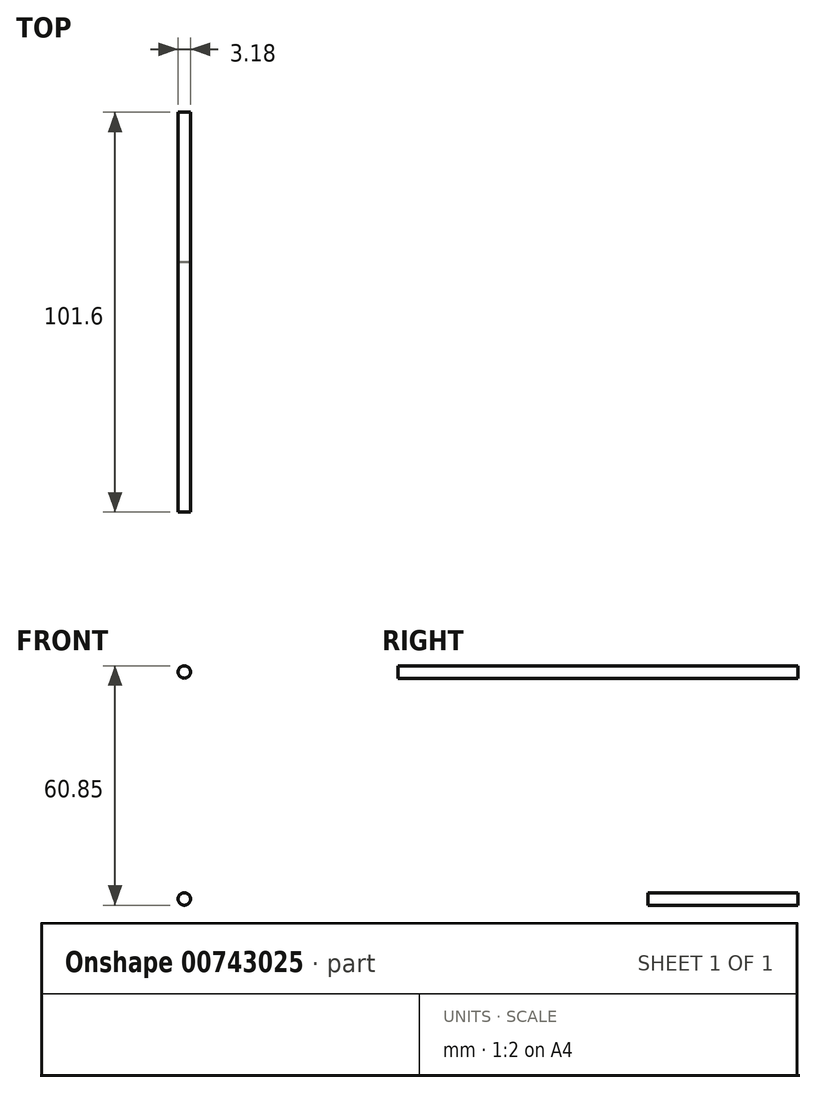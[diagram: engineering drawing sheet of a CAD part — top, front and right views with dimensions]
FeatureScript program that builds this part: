
annotation { "Feature Type Name" : "Feature", "Feature Type Description" : "" }
export const myFeature = defineFeature(function(context is Context, id is Id, definition is map)
    precondition{}
    {
        {
            var Q0;
            Q0=qCreatedBy(makeId("Front.planeOp"),FACE);
            var sketch = newSketch(context, id + "F0", { "sketchPlane" : qUnion([Q0])});
            skLineSegment(sketch, "E0", {"start": v(0, 0) * mm, "end": v(0, 8.52) * mm});
            skCircle(sketch, "E1", {"center": v(0, 8.52) * mm, "radius": 1.59 * mm});
            skLineSegment(sketch, "E2", {"start": v(0, 0) * mm, "end": v(0, -27.75) * mm});
            skCircle(sketch, "E3", {"center": v(0, -27.75) * mm, "radius": 1.59 * mm});
            skLineSegment(sketch, "E4", {"start": v(0, -27.75) * mm, "end": v(0, -49.15) * mm});
            skCircle(sketch, "E5", {"center": v(0, -49.15) * mm, "radius": 1.59 * mm});
            skSolve(sketch);
        }
        {
            var Q0;
            Q0=makeQuery(id+"F0.imprint","IMPRINT",FACE,{"disambiguationData":[TD([[makeQuery(id+"F0.imprint","IMPRINT",EDGE,{"derivedFrom":sQuery(id+"F0.wireOp",EDGE,"E1")}),1.0]])]});
            extrude(context, id + "F1", {"entities" : qUnion([Q0]), "depth" : 101.6 * mm, "offsetDistance" : 25.4 * mm});
        }
        {
            var Q0;
            Q0=makeQuery(id+"F0.imprint","IMPRINT",FACE,{"disambiguationData":[TD([[makeQuery(id+"F0.imprint","IMPRINT",EDGE,{"derivedFrom":sQuery(id+"F0.wireOp",EDGE,"E5")}),1.0]])]});
            extrude(context, id + "F2", {"entities" : qUnion([Q0]), "depth" : 38.1 * mm, "offsetDistance" : 25.4 * mm});
        }
        {
            var Q0;
            Q0=sQuery(id+"F0.wireOp",EDGE,"E3");
            extrude(context, id + "F3", {"bodyType" : ToolBodyType.SURFACE, "surfaceEntities" : qUnion([Q0]), "depth" : 63.5 * mm, "offsetDistance" : 25.4 * mm});
        }
    });
